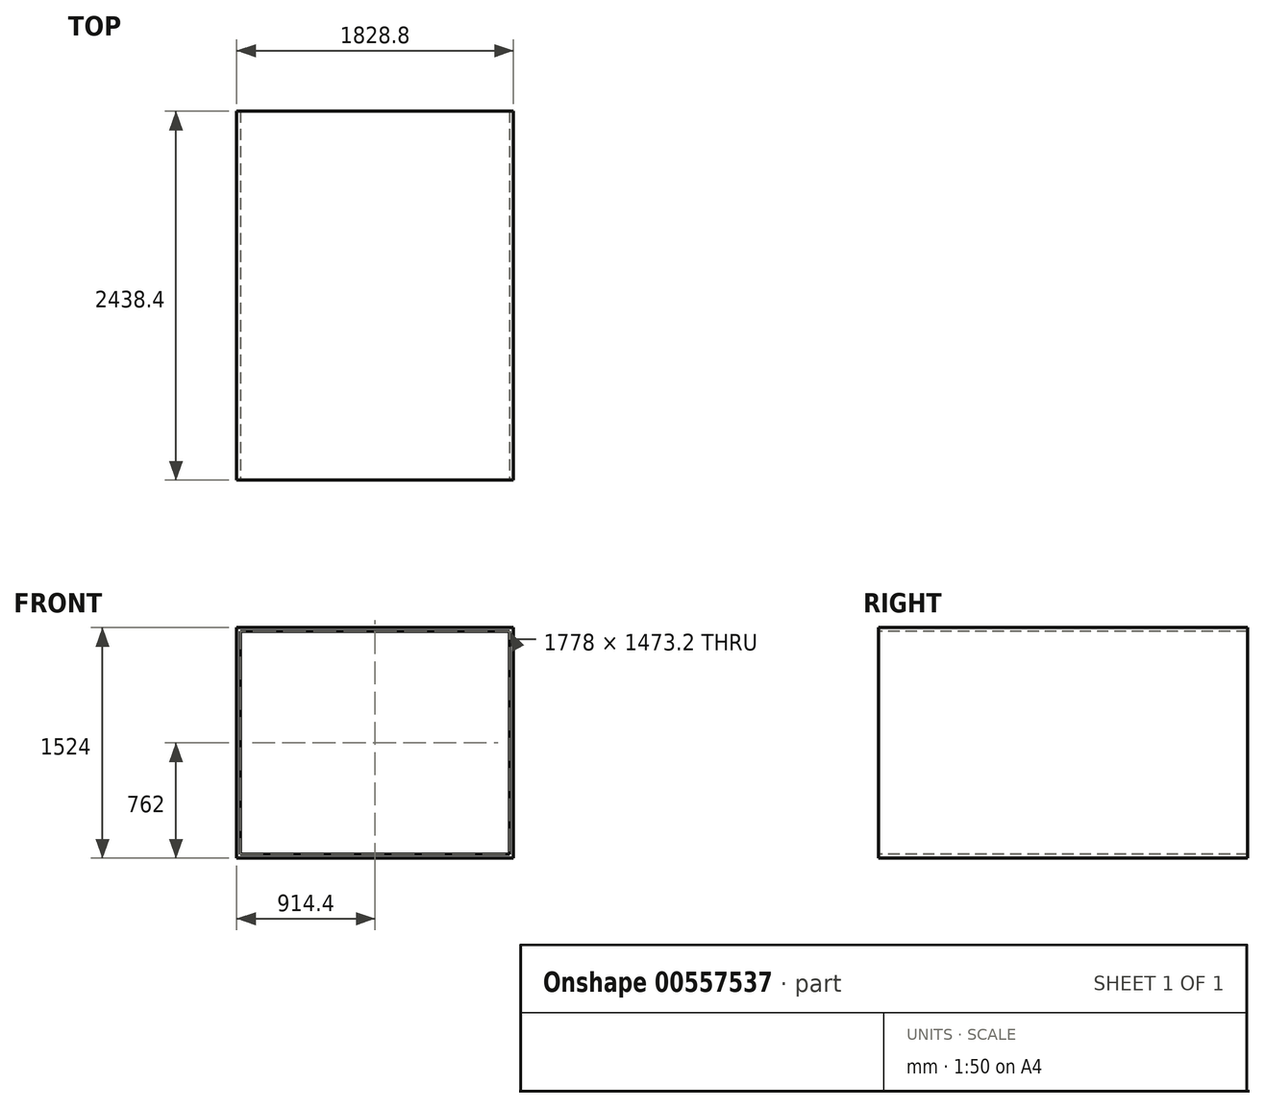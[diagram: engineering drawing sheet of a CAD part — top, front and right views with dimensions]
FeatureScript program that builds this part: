
annotation { "Feature Type Name" : "Feature", "Feature Type Description" : "" }
export const myFeature = defineFeature(function(context is Context, id is Id, definition is map)
    precondition{}
    {
        {
            var Q0;
            Q0=qCreatedBy(makeId("Front.planeOp"),FACE);
            var sketch = newSketch(context, id + "F0", { "sketchPlane" : qUnion([Q0])});
            skLineSegment(sketch, "E0.bottom", {"start": v(914.4, 762) * mm, "end": v(-914.4, 762) * mm});
            skLineSegment(sketch, "E0.top", {"start": v(914.4, -762) * mm, "end": v(-914.4, -762) * mm});
            skLineSegment(sketch, "E0.left", {"start": v(914.4, 762) * mm, "end": v(914.4, -762) * mm});
            skLineSegment(sketch, "E0.right", {"start": v(-914.4, 762) * mm, "end": v(-914.4, -762) * mm});
            skPoint(sketch, "E0.middle", {"position": v(0, 0) * mm});
            skLineSegment(sketch, "E1.bottom", {"start": v(889, -736.6) * mm, "end": v(-889, -736.6) * mm});
            skLineSegment(sketch, "E1.top", {"start": v(889, 736.6) * mm, "end": v(-889, 736.6) * mm});
            skLineSegment(sketch, "E1.left", {"start": v(889, -736.6) * mm, "end": v(889, 736.6) * mm});
            skLineSegment(sketch, "E1.right", {"start": v(-889, -736.6) * mm, "end": v(-889, 736.6) * mm});
            skSolve(sketch);
        }
        {
            var Q0;
            Q0 = qSketchRegion(id + "F0", true);
            extrude(context, id + "F1", {"entities" : qUnion([Q0]), "oppositeDirection" : true, "depth" : 2438.4 * mm, "offsetDistance" : 25.4 * mm});
        }
    });
